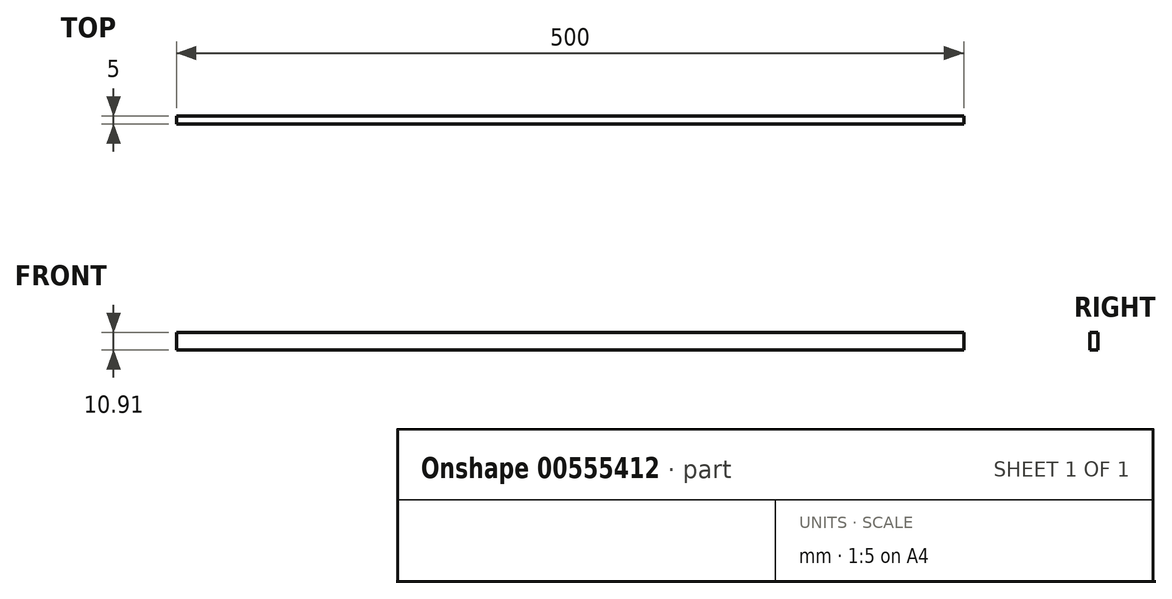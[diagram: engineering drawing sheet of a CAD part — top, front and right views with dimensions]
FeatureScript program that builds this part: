
annotation { "Feature Type Name" : "Feature", "Feature Type Description" : "" }
export const myFeature = defineFeature(function(context is Context, id is Id, definition is map)
    precondition{}
    {
        {
            var Q0;
            Q0=qCreatedBy(makeId("Front.planeOp"),FACE);
            var sketch = newSketch(context, id + "F0", { "sketchPlane" : qUnion([Q0])});
            skLineSegment(sketch, "E0.bottom", {"start": v(0, 0) * mm, "end": v(-500, 0) * mm});
            skLineSegment(sketch, "E0.top", {"start": v(0, -10.9) * mm, "end": v(-500, -10.9) * mm});
            skLineSegment(sketch, "E0.left", {"start": v(0, 0) * mm, "end": v(0, -10.9) * mm});
            skLineSegment(sketch, "E0.right", {"start": v(-500, 0) * mm, "end": v(-500, -10.9) * mm});
            skSolve(sketch);
        }
        {
            var Q0;
            Q0=makeQuery(id+"F0.imprint","IMPRINT",FACE,{"disambiguationData":[TD([[makeQuery(id+"F0.imprint","IMPRINT",EDGE,{"derivedFrom":sQuery(id+"F0.wireOp",EDGE,"E0.bottom")}),1.0]])]});
            extrude(context, id + "F1", {"entities" : qUnion([Q0]), "depth" : 5 * mm, "offsetDistance" : 25 * mm});
        }
    });
